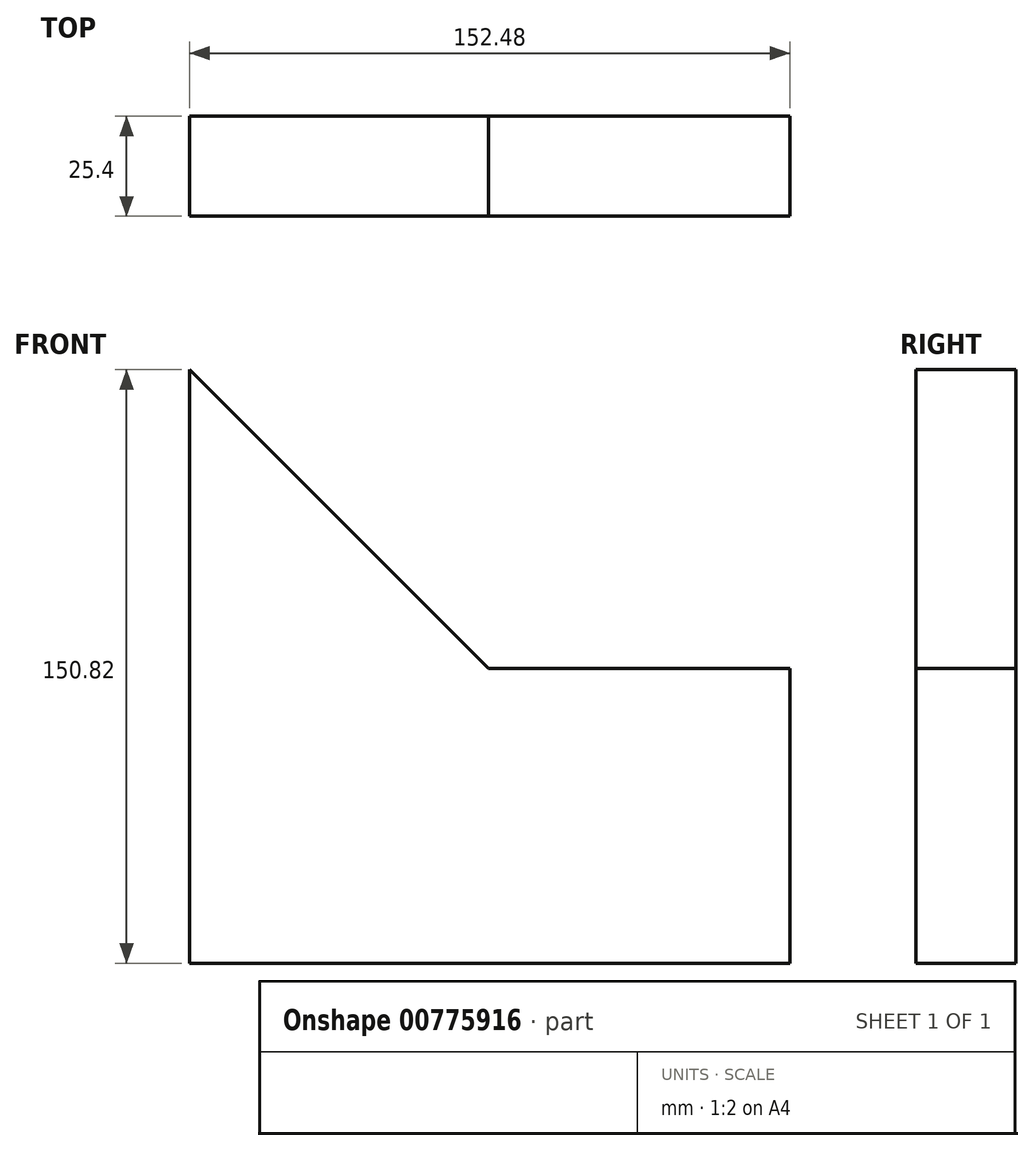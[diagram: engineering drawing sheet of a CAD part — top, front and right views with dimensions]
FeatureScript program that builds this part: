
annotation { "Feature Type Name" : "Feature", "Feature Type Description" : "" }
export const myFeature = defineFeature(function(context is Context, id is Id, definition is map)
    precondition{}
    {
        {
            var Q0;
            Q0=qCreatedBy(makeId("Front.planeOp"),FACE);
            var sketch = newSketch(context, id + "F0", { "sketchPlane" : qUnion([Q0])});
            skLineSegment(sketch, "E0", {"start": v(-75.93, 75.93) * mm, "end": v(-75.93, -74.9) * mm});
            skLineSegment(sketch, "E1", {"start": v(-75.93, -74.9) * mm, "end": v(76.55, -74.9) * mm});
            skLineSegment(sketch, "E2", {"start": v(76.55, -74.9) * mm, "end": v(76.55, 0) * mm});
            skLineSegment(sketch, "E3", {"start": v(76.55, 0) * mm, "end": v(0, 0) * mm});
            skLineSegment(sketch, "E4", {"start": v(0, 0) * mm, "end": v(-75.93, 75.93) * mm});
            skSolve(sketch);
        }
        {
            var Q0;
            Q0=makeQuery(id+"F0.imprint","IMPRINT",FACE,{"disambiguationData":[TD([[makeQuery(id+"F0.imprint","IMPRINT",EDGE,{"derivedFrom":sQuery(id+"F0.wireOp",EDGE,"E0")}),1.0]])]});
            extrude(context, id + "F1", {"entities" : qUnion([Q0]), "depth" : 25.4 * mm, "offsetDistance" : 25.4 * mm});
        }
    });
